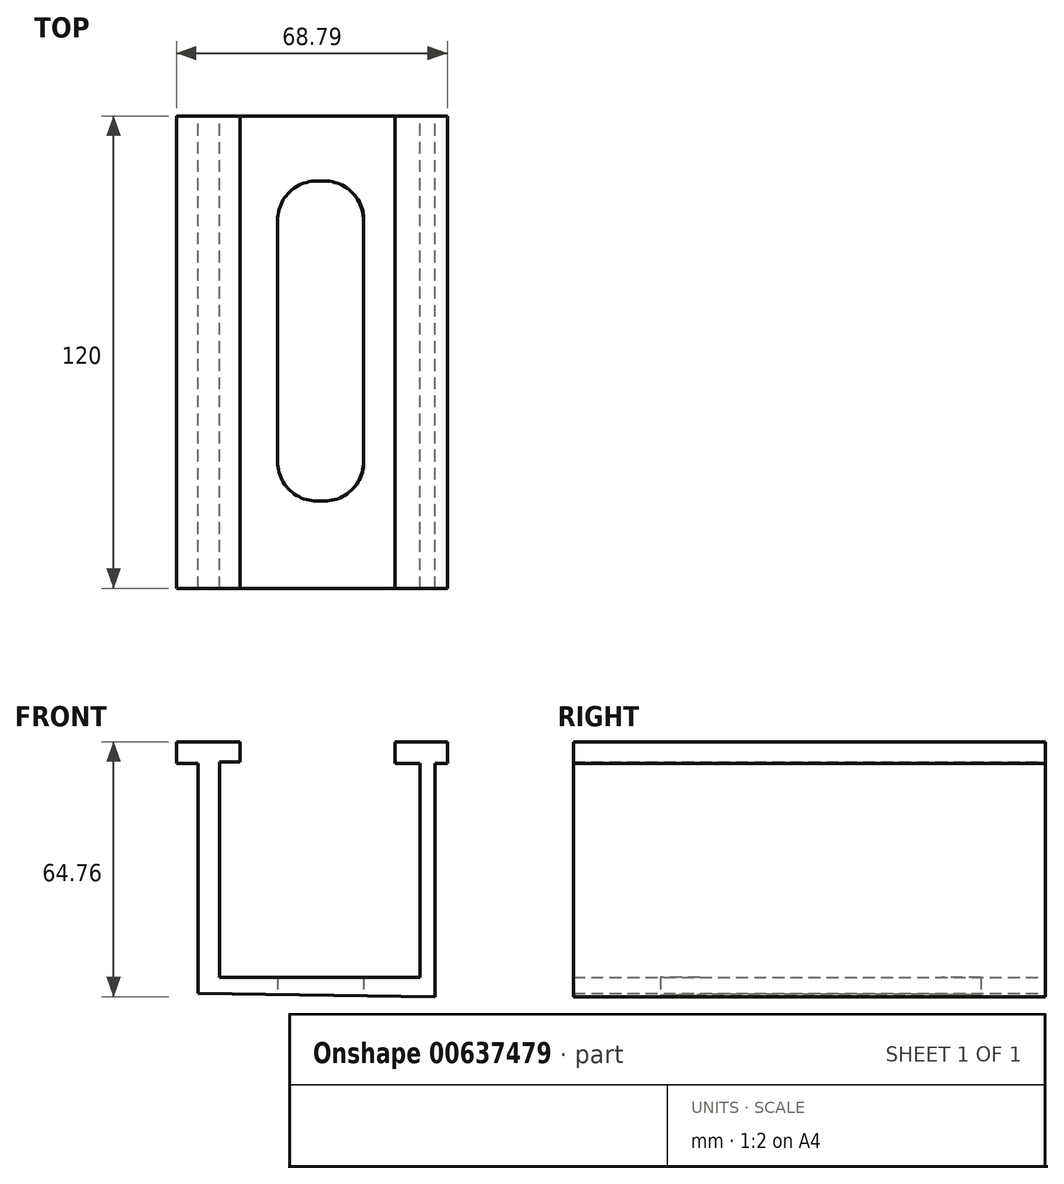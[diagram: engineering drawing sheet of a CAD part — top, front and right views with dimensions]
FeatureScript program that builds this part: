
annotation { "Feature Type Name" : "Feature", "Feature Type Description" : "" }
export const myFeature = defineFeature(function(context is Context, id is Id, definition is map)
    precondition{}
    {
        {
            var Q0;
            Q0=qCreatedBy(makeId("Front.planeOp"),FACE);
            var sketch = newSketch(context, id + "F0", { "sketchPlane" : qUnion([Q0])});
            skLineSegment(sketch, "E0", {"start": v(-31.8, 34.68) * mm, "end": v(-47.92, 34.68) * mm});
            skLineSegment(sketch, "E1", {"start": v(-47.92, 34.68) * mm, "end": v(-47.92, 29.21) * mm});
            skLineSegment(sketch, "E2", {"start": v(-47.92, 29.21) * mm, "end": v(-42.45, 29.21) * mm});
            skLineSegment(sketch, "E3", {"start": v(-42.45, 29.21) * mm, "end": v(-42.45, -29.21) * mm});
            skLineSegment(sketch, "E4", {"start": v(-31.8, 34.68) * mm, "end": v(-31.8, 29.5) * mm});
            skLineSegment(sketch, "E5", {"start": v(-31.8, 29.5) * mm, "end": v(-36.98, 29.5) * mm});
            skLineSegment(sketch, "E6", {"start": v(-36.98, 29.5) * mm, "end": v(-36.98, -25.18) * mm});
            skLineSegment(sketch, "E7", {"start": v(-36.98, -25.18) * mm, "end": v(13.96, -25.18) * mm});
            skLineSegment(sketch, "E8", {"start": v(13.96, -25.18) * mm, "end": v(13.96, 29.21) * mm});
            skLineSegment(sketch, "E9", {"start": v(13.96, 29.21) * mm, "end": v(7.63, 29.21) * mm});
            skLineSegment(sketch, "E10", {"start": v(7.63, 29.21) * mm, "end": v(7.63, 34.68) * mm});
            skLineSegment(sketch, "E11", {"start": v(7.63, 34.68) * mm, "end": v(20.87, 34.68) * mm});
            skLineSegment(sketch, "E12", {"start": v(20.87, 34.68) * mm, "end": v(20.87, 29.21) * mm});
            skLineSegment(sketch, "E13", {"start": v(20.87, 29.21) * mm, "end": v(17.7, 29.21) * mm});
            skLineSegment(sketch, "E14", {"start": v(17.7, 29.21) * mm, "end": v(17.7, -30.08) * mm});
            skLineSegment(sketch, "E15", {"start": v(17.7, -30.08) * mm, "end": v(-42.45, -29.21) * mm});
            skSolve(sketch);
        }
        {
            var Q0;
            Q0 = qSketchRegion(id + "F0", true);
            extrude(context, id + "F1", {"entities" : qUnion([Q0]), "depth" : 120 * mm, "offsetDistance" : 25 * mm});
        }
        {
            var Q0;
            Q0=makeQuery(id+"F1.opExtrude","SWEPT_FACE",FACE,{"disambiguationData":[OSD([sQuery(id+"F0.wireOp",EDGE,"E15")])]});
            var sketch = newSketch(context, id + "F2", { "sketchPlane" : qUnion([Q0])});
            skPoint(sketch, "E16.start.orphan", {"position": v(0, 107.03) * mm});
            skLineSegment(sketch, "E17.bottom", {"start": v(-11.9, 97.83) * mm, "end": v(-10, 97.83) * mm});
            skLineSegment(sketch, "E17.top", {"start": v(-11.9, 16.5) * mm, "end": v(-10, 16.5) * mm});
            skPoint(sketch, "E18.visualSharp", {"position": v(-21.9, 97.83) * mm});
            skPoint(sketch, "E19.visualSharp", {"position": v(0, 97.83) * mm});
            skPoint(sketch, "E20.visualSharp", {"position": v(-21.9, 16.5) * mm});
            skPoint(sketch, "E21.visualSharp", {"position": v(0, 16.5) * mm});
            skLineSegment(sketch, "E22.left", {"start": v(-21.9, 26.5) * mm, "end": v(-21.9, 87.83) * mm});
            skLineSegment(sketch, "E22.right", {"start": v(0, 26.5) * mm, "end": v(0, 87.83) * mm});
            skArc(sketch, "E23.filletArc", {"start": v(-21.9, 26.5) * mm, "mid": v(-18.97, 19.42) * mm, "end": v(-11.9, 16.5) * mm});
            skArc(sketch, "E24.filletArc", {"start": v(-10, 16.5) * mm, "mid": v(-2.93, 19.42) * mm, "end": v(0, 26.5) * mm});
            skArc(sketch, "E25.filletArc", {"start": v(-11.9, 97.83) * mm, "mid": v(-18.97, 94.9) * mm, "end": v(-21.9, 87.83) * mm});
            skArc(sketch, "E26.filletArc", {"start": v(0, 87.83) * mm, "mid": v(-2.93, 94.9) * mm, "end": v(-10, 97.83) * mm});
            skSolve(sketch);
        }
        {
            var Q0;
            Q0=makeQuery(id+"F2.imprint","IMPRINT",FACE,{"disambiguationData":[TD([[makeQuery(id+"F2.imprint","IMPRINT",EDGE,{"derivedFrom":sQuery(id+"F2.wireOp",EDGE,"E17.top")}),1.0]])]});
            extrude(context, id + "F3", {"entities" : qUnion([Q0]), "operationType" : NewBodyOperationType.REMOVE, "depth" : 25 * mm, "offsetDistance" : 25 * mm});
        }
        {
            var Q0;
            Q0 = qSketchRegion(id + "F2", true);
            extrude(context, id + "F4", {"entities" : qUnion([Q0]), "operationType" : NewBodyOperationType.REMOVE, "oppositeDirection" : true, "depth" : 25 * mm, "offsetDistance" : 25 * mm});
        }
    });
